# Revit family: Shower-Showerhead-KOHLER-Bancroft-K-14519
name_source: partatom
category: Plumbing Fixtures
revit_build: Autodesk Revit 2015 (Build: 20140606_1530(x64)
units: mm (PartAtom-declared; Revit-internal decimal feet)

## types (10) — shared parameters
ADA Compliant = No
Assembly Code = D2010700
CW Connection = No
Cold Water Inlet = Cold Water Inlet
Date Modified = 04/02/2019
Default Elevation = 0"
Drain Included = No
Flow Rate = 2 GPM
HW Connection = Yes
Height = 4 13/16"
Hot Water Inlet = Hot Water Inlet
Length = 5 15/16"
Manufacturer = KOHLER Co.
MasterFormat 1995 = 15410
MasterFormat 2004 = 22.41.23
Material = Premium Metal Construction
Panel Thickness = 0"
Pressure = 80.00 psi
Product Documentation Link = https://www.us.kohler.com
Product Name = Bancroft
Product Page URL = http://www.us.kohler.com
Tempered Water Inlet = Tempered Water Inlet
URL = https://www.us.kohler.com
Vent Connection = No
Waste Connection = No
Waste Water Outlet = Waste Water Outlet
WaterSense Certified = Yes
Width = 5 15/16"

## per-type parameters (varying)
| type | Description | Finish | Model | Type |
| 1.75 GPM, CP-Polished Chrome | 1.75 gpm single-function showerhead with Katalyst air-induction technology | Kohler-Metal-CP-Polished_Chrome | K-14519-G-CP | 1 |
| 1.75 GPM, SN-Vibrant Polished Nickel | 1.75 gpm single-function showerhead with Katalyst air-induction technology | Kohler-Metal-SN-Vibrant_Polished_Nickel | K-14519-G-SN | 2 |
| 1.75 GPM, BN-Vibrant Brushed Nickel | 1.75 gpm single-function showerhead with Katalyst air-induction technology | Kohler-Metal-BN-Vibrant_Brushed_Nickel | K-14519-G-BN | 3 |
| 1.75 GPM, BV-Vibrant Brushed Bronze | 1.75 gpm single-function showerhead with Katalyst air-induction technology | Kohler-Metal-BV-Brushed_Bronze | K-14519-G-BV | 4 |
| 1.75 GPM, 2BZ-Oil Rubbed Bronze | 1.75 gpm single-function showerhead with Katalyst air-induction technology | Kohler-Metal-2BZ-Oil_Rubbed_Bronze | K-14519-G-2BZ | 5 |
| 2 GPM, CP-Polished Chrome | 2.0 gpm single-function showerhead with Katalyst air-induction technology | Kohler-Metal-CP-Polished_Chrome | K-14519-CP | 6 |
| 2 GPM, SN-Vibrant Polished Nickel | 2.0 gpm single-function showerhead with Katalyst air-induction technology | Kohler-Metal-SN-Vibrant_Polished_Nickel | K-14519-SN | 7 |
| 2 GPM, BN-Vibrant Brushed Nickel | 2.0 gpm single-function showerhead with Katalyst air-induction technology | Kohler-Metal-BN-Vibrant_Brushed_Nickel | K-14519-BN | 8 |
| 2 GPM, BV-Vibrant Brushed Bronze | 2.0 gpm single-function showerhead with Katalyst air-induction technology | Kohler-Metal-BV-Brushed_Bronze | K-14519-BV | 9 |
| 2 GPM, 2BZ-Oil Rubbed Bronze | 2.0 gpm single-function showerhead with Katalyst air-induction technology | Kohler-Metal-2BZ-Oil_Rubbed_Bronze | K-14519-2BZ | 10 |

## geometry (parser evidence)
native form markers: Sweep x5
no freeform markers — native parametric forms only
